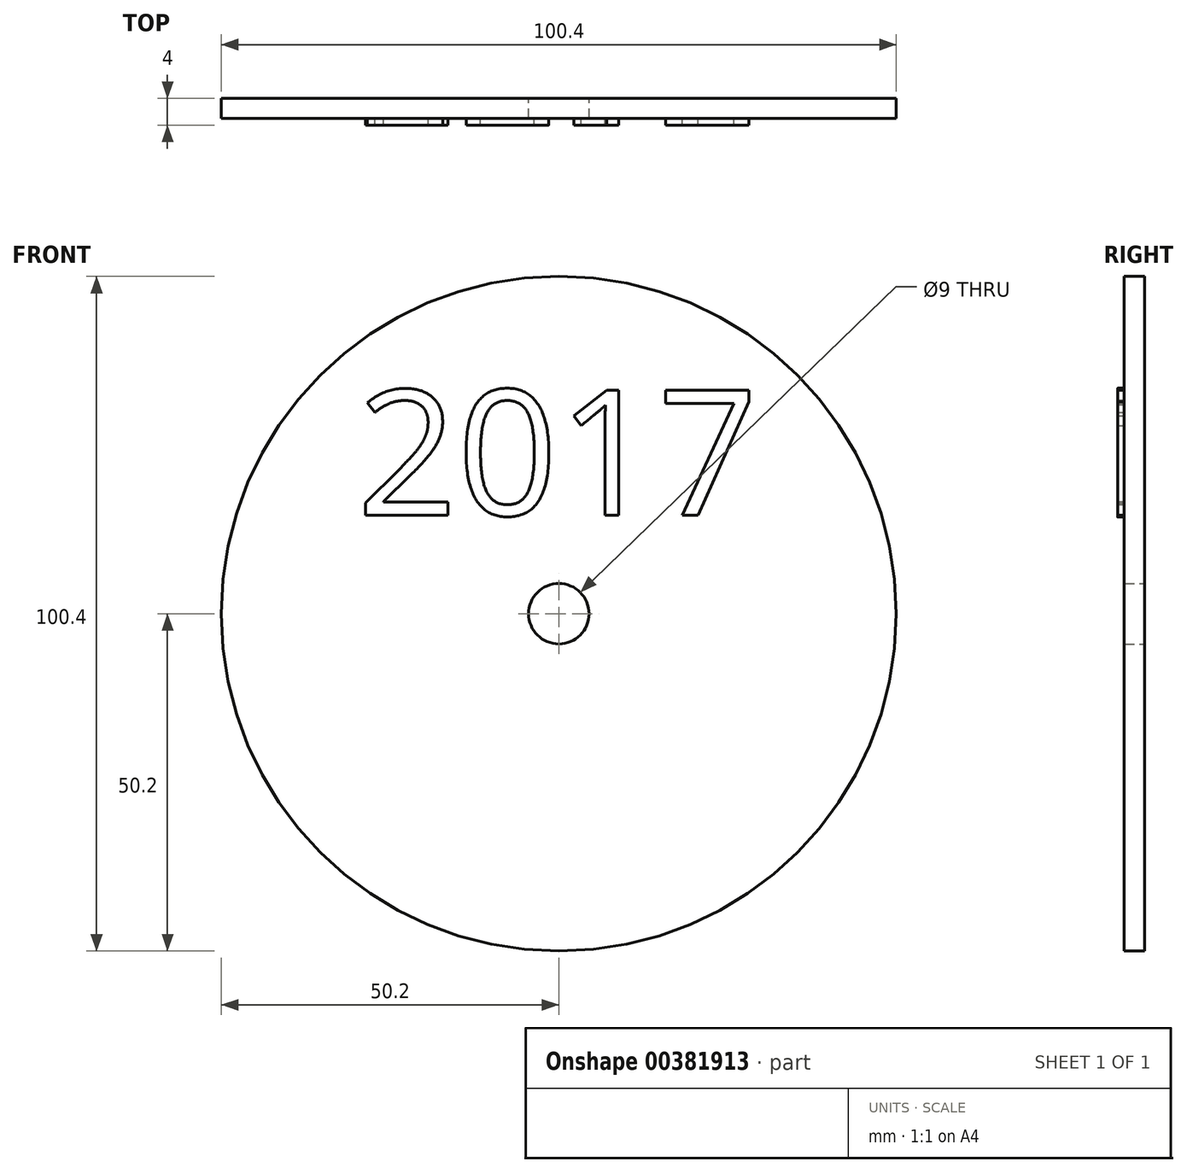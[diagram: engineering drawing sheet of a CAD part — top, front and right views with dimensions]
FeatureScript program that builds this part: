
annotation { "Feature Type Name" : "Feature", "Feature Type Description" : "" }
export const myFeature = defineFeature(function(context is Context, id is Id, definition is map)
    precondition{}
    {
        {
            var Q0;
            Q0=qCreatedBy(makeId("Front.planeOp"),FACE);
            var sketch = newSketch(context, id + "F0", { "sketchPlane" : qUnion([Q0])});
            skCircle(sketch, "E0", {"center": v(0, 0) * mm, "radius": 50.2 * mm});
            skCircle(sketch, "E1", {"center": v(0, 0) * mm, "radius": 4.5 * mm});
            skSolve(sketch);
        }
        {
            var Q0;
            Q0=makeQuery(id+"F0.imprint","IMPRINT",FACE,{"disambiguationData":[TD([[makeQuery(id+"F0.imprint","IMPRINT",EDGE,{"derivedFrom":sQuery(id+"F0.wireOp",EDGE,"E0")}),1.0]])]});
            extrude(context, id + "F1", {"entities" : qUnion([Q0]), "depth" : 3 * mm});
        }
        {
            var Q0;
            Q0=makeQuery(id+"F1.opExtrude","CAP_FACE",FACE,{"disambiguationData":[OSD([sQuery(id+"F0.wireOp",EDGE,"E0"),sQuery(id+"F0.wireOp",EDGE,"E1")])],"isStart":false});
            var sketch = newSketch(context, id + "F2", { "sketchPlane" : qUnion([Q0])});
            skCircle(sketch, "E2", {"center": v(0, 0) * mm, "radius": 4.5 * mm});
            skSolve(sketch);
        }
        {
            var Q0;
            Q0=sQuery(id+"F2.wireOp",EDGE,"E2");
            extrude(context, id + "F3", {"bodyType" : ToolBodyType.SURFACE, "surfaceEntities" : qUnion([Q0]), "depth" : 100 * mm});
        }
        {
            var Q0;
            Q0=makeQuery(id+"F1.opExtrude","CAP_FACE",FACE,{"disambiguationData":[OSD([sQuery(id+"F0.wireOp",EDGE,"E0"),sQuery(id+"F0.wireOp",EDGE,"E1")])],"isStart":false});
            var sketch = newSketch(context, id + "F4", { "sketchPlane" : qUnion([Q0])});
            skText(sketch, "E3", { "text": "2017\n", "fontName": "OpenSans-Regular.ttf"});
            const initialGuessF4  = {"E3": [-0.03, 0.01466, 1, 0, 0.01877]};
            skSetInitialGuess(sketch, initialGuessF4);
            skSolve(sketch);
        }
        {
            var Q0;
            Q0 = qSketchRegion(id + "F4", true);
            extrude(context, id + "F5", {"entities" : qUnion([Q0]), "operationType" : NewBodyOperationType.ADD, "depth" : 1 * mm});
        }
    });
